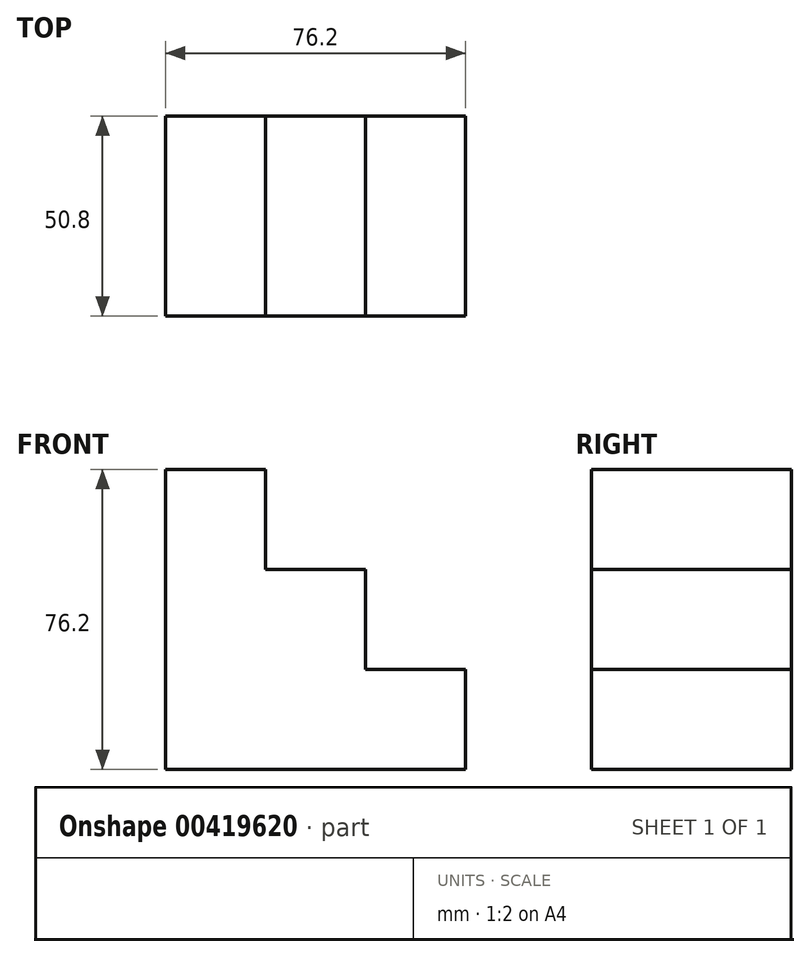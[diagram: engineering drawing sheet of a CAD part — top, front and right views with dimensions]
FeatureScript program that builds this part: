
annotation { "Feature Type Name" : "Feature", "Feature Type Description" : "" }
export const myFeature = defineFeature(function(context is Context, id is Id, definition is map)
    precondition{}
    {
        {
            var Q0;
            Q0=qCreatedBy(makeId("Front.planeOp"),FACE);
            var sketch = newSketch(context, id + "F0", { "sketchPlane" : qUnion([Q0])});
            skLineSegment(sketch, "E0", {"start": v(0, 0) * mm, "end": v(-76.2, 0) * mm});
            skLineSegment(sketch, "E1", {"start": v(-76.2, 0) * mm, "end": v(-76.2, 76.2) * mm});
            skLineSegment(sketch, "E2", {"start": v(-76.2, 76.2) * mm, "end": v(-50.8, 76.2) * mm});
            skLineSegment(sketch, "E3", {"start": v(-50.8, 76.2) * mm, "end": v(-50.8, 50.8) * mm});
            skLineSegment(sketch, "E4", {"start": v(-50.8, 50.8) * mm, "end": v(-25.4, 50.8) * mm});
            skLineSegment(sketch, "E5", {"start": v(-25.4, 50.8) * mm, "end": v(-25.4, 25.4) * mm});
            skLineSegment(sketch, "E6", {"start": v(-25.4, 25.4) * mm, "end": v(0, 25.4) * mm});
            skLineSegment(sketch, "E7", {"start": v(0, 25.4) * mm, "end": v(0, 0) * mm});
            skSolve(sketch);
        }
        {
            var Q0;
            Q0 = qSketchRegion(id + "F0", true);
            extrude(context, id + "F1", {"entities" : qUnion([Q0]), "depth" : 50.8 * mm});
        }
    });
